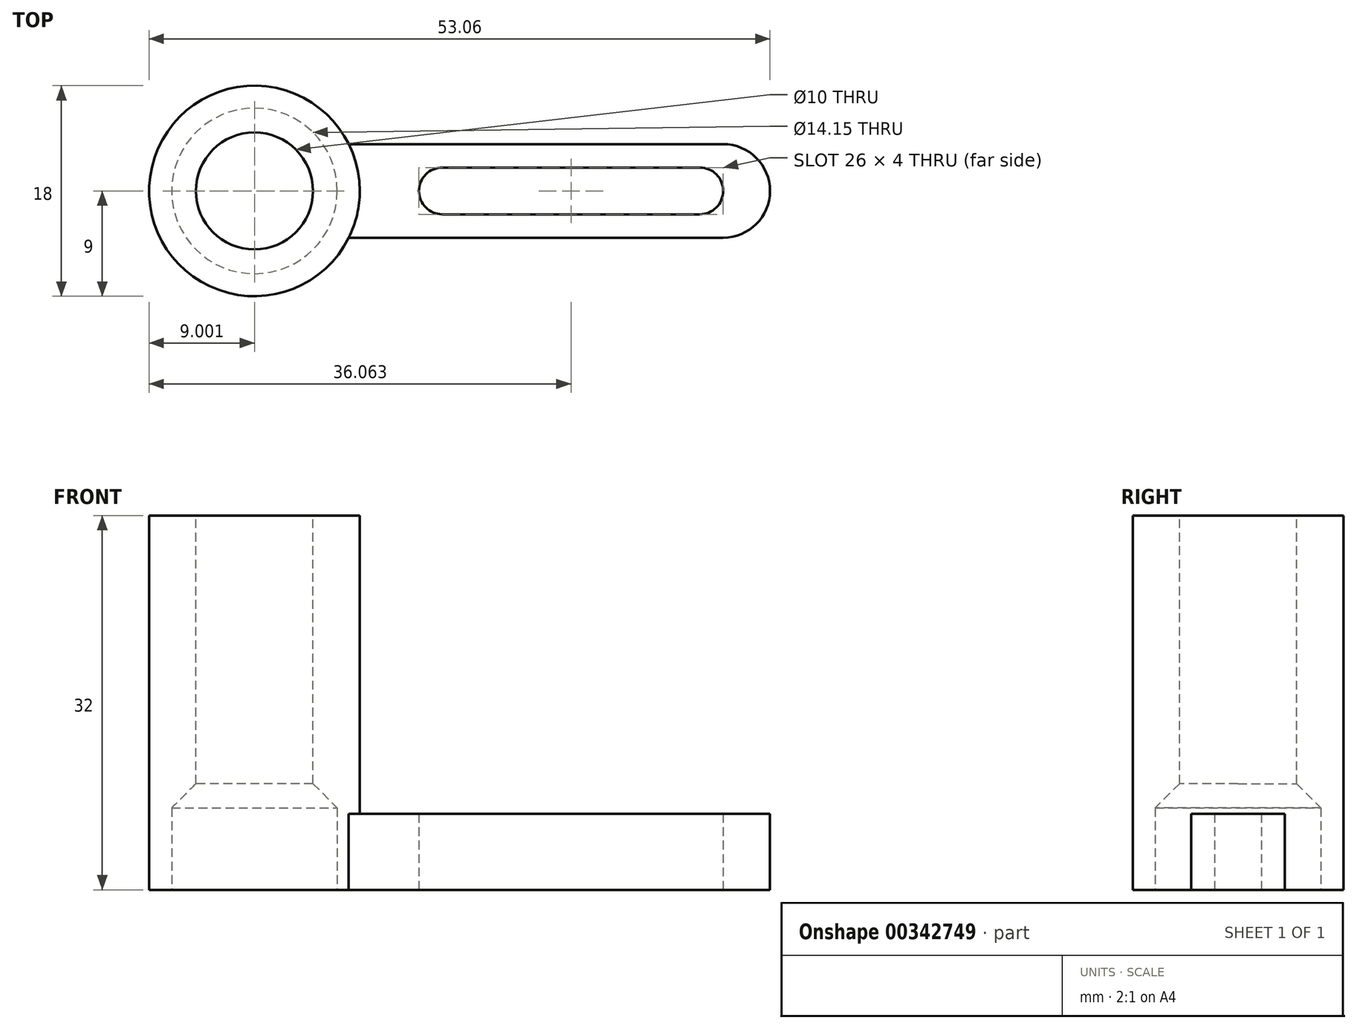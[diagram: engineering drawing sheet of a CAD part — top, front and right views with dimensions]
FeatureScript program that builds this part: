
annotation { "Feature Type Name" : "Feature", "Feature Type Description" : "" }
export const myFeature = defineFeature(function(context is Context, id is Id, definition is map)
    precondition{}
    {
        {
            var Q0;
            Q0=qCreatedBy(makeId("Top.planeOp"),FACE);
            var sketch = newSketch(context, id + "F0", { "sketchPlane" : qUnion([Q0])});
            skLineSegment(sketch, "E0", {"start": v(-60.74, 4) * mm, "end": v(-28.74, 4) * mm});
            skArc(sketch, "E1", {"start": v(-28.74, 4) * mm, "mid": v(-25.9, 2.83) * mm, "end": v(-24.74, 0) * mm});
            skLineSegment(sketch, "E2", {"start": v(-52.74, 2) * mm, "end": v(-30.74, 2) * mm});
            skArc(sketch, "E3", {"start": v(-54.74, 0) * mm, "mid": v(-54.15, 1.41) * mm, "end": v(-52.74, 2) * mm});
            skArc(sketch, "E4", {"start": v(-28.74, 0) * mm, "mid": v(-29.32, 1.41) * mm, "end": v(-30.74, 2) * mm});
            skArc(sketch, "E5", {"start": v(-60.74, 4) * mm, "mid": v(-70.85, 8.76) * mm, "end": v(-77.8, 0) * mm});
            skArc(sketch, "E6.MirrorCS", {"start": v(-60.74, -4) * mm, "mid": v(-70.85, -8.76) * mm, "end": v(-77.8, 0) * mm});
            skLineSegment(sketch, "E7.MirrorCS", {"start": v(-60.74, -4) * mm, "end": v(-28.74, -4) * mm});
            skArc(sketch, "E8.MirrorCS", {"start": v(-28.74, -4) * mm, "mid": v(-25.9, -2.83) * mm, "end": v(-24.74, 0) * mm});
            skArc(sketch, "E9.MirrorCS", {"start": v(-28.74, 0) * mm, "mid": v(-29.32, -1.41) * mm, "end": v(-30.74, -2) * mm});
            skLineSegment(sketch, "E10.MirrorCS", {"start": v(-52.74, -2) * mm, "end": v(-30.74, -2) * mm});
            skArc(sketch, "E11.MirrorCS", {"start": v(-54.74, 0) * mm, "mid": v(-54.15, -1.41) * mm, "end": v(-52.74, -2) * mm});
            skSolve(sketch);
        }
        {
            var Q0;
            Q0=makeQuery(id+"F0.imprint","IMPRINT",FACE,{"disambiguationData":[TD([[makeQuery(id+"F0.imprint","IMPRINT",EDGE,{"derivedFrom":sQuery(id+"F0.wireOp",EDGE,"E0")}),-1.0]])]});
            extrude(context, id + "F1", {"entities" : qUnion([Q0]), "depth" : 6.5 * mm});
        }
        {
            var Q0;
            Q0=makeQuery(id+"F1.opExtrude","CAP_FACE",FACE,{"disambiguationData":[OSD([sQuery(id+"F0.wireOp",EDGE,"E0"),sQuery(id+"F0.wireOp",EDGE,"E1"),sQuery(id+"F0.wireOp",EDGE,"E2"),sQuery(id+"F0.wireOp",EDGE,"E3"),sQuery(id+"F0.wireOp",EDGE,"E4"),sQuery(id+"F0.wireOp",EDGE,"E5"),sQuery(id+"F0.wireOp",EDGE,"E6.MirrorCS"),sQuery(id+"F0.wireOp",EDGE,"E7.MirrorCS"),sQuery(id+"F0.wireOp",EDGE,"E8.MirrorCS"),sQuery(id+"F0.wireOp",EDGE,"E9.MirrorCS"),sQuery(id+"F0.wireOp",EDGE,"E10.MirrorCS"),sQuery(id+"F0.wireOp",EDGE,"E11.MirrorCS")])],"isStart":false});
            var sketch = newSketch(context, id + "F2", { "sketchPlane" : qUnion([Q0])});
            skCircle(sketch, "E12", {"center": v(-68.8, 0) * mm, "radius": 9 * mm});
            skSolve(sketch);
        }
        {
            var Q0;
            {var subQ0=sQuery(id+"F2.wireOp",EDGE,"E12");var subQ1=makeQuery(id+"F2.imprint","INTERSECT",VERTEX,{"derivedFrom":[makeQuery(id+"F1.opExtrude","CAP_EDGE",EDGE,{"disambiguationData":[OSD([sQuery(id+"F0.wireOp",EDGE,"E0")])],"isStart":false}),subQ0]});Q0=makeQuery(id+"F2.imprint","IMPRINT",FACE,{"disambiguationData":[TD([[makeQuery(id+"F2.imprint","IMPRINT",EDGE,{"disambiguationData":[TD([[subQ1,-1.0]])],"derivedFrom":subQ0}),1.0]])]});}
            extrude(context, id + "F3", {"entities" : qUnion([Q0]), "operationType" : NewBodyOperationType.ADD, "depth" : 25.5 * mm});
        }
        {
            var Q0;
            Q0=makeQuery(id+"F3.opExtrude","CAP_FACE",FACE,{"disambiguationData":[OSD([sQuery(id+"F2.wireOp",EDGE,"E12")])],"isStart":false});
            var sketch = newSketch(context, id + "F4", { "sketchPlane" : qUnion([Q0])});
            skCircle(sketch, "E13", {"center": v(-68.8, 0) * mm, "radius": 5 * mm});
            skSolve(sketch);
        }
        {
            var Q0;
            Q0=makeQuery(id+"F4.imprint","IMPRINT",FACE,{"disambiguationData":[TD([[makeQuery(id+"F4.imprint","IMPRINT",EDGE,{"derivedFrom":sQuery(id+"F4.wireOp",EDGE,"E13")}),1.0]])]});
            var Q1;
            Q1=makeQuery(id+"F1.opExtrude","CAP_FACE",FACE,{"disambiguationData":[OSD([sQuery(id+"F0.wireOp",EDGE,"E0"),sQuery(id+"F0.wireOp",EDGE,"E1"),sQuery(id+"F0.wireOp",EDGE,"E2"),sQuery(id+"F0.wireOp",EDGE,"E3"),sQuery(id+"F0.wireOp",EDGE,"E4"),sQuery(id+"F0.wireOp",EDGE,"E5"),sQuery(id+"F0.wireOp",EDGE,"E6.MirrorCS"),sQuery(id+"F0.wireOp",EDGE,"E7.MirrorCS"),sQuery(id+"F0.wireOp",EDGE,"E8.MirrorCS"),sQuery(id+"F0.wireOp",EDGE,"E9.MirrorCS"),sQuery(id+"F0.wireOp",EDGE,"E10.MirrorCS"),sQuery(id+"F0.wireOp",EDGE,"E11.MirrorCS")])],"isStart":true});
            var Q2;
            Q2=makeQuery(id+"F1.opExtrude","SWEPT_BODY",BODY,{"disambiguationData":[OSD([sQuery(id+"F0.wireOp",EDGE,"E0"),sQuery(id+"F0.wireOp",EDGE,"E1"),sQuery(id+"F0.wireOp",EDGE,"E2"),sQuery(id+"F0.wireOp",EDGE,"E3"),sQuery(id+"F0.wireOp",EDGE,"E4"),sQuery(id+"F0.wireOp",EDGE,"E5"),sQuery(id+"F0.wireOp",EDGE,"E6.MirrorCS"),sQuery(id+"F0.wireOp",EDGE,"E7.MirrorCS"),sQuery(id+"F0.wireOp",EDGE,"E8.MirrorCS"),sQuery(id+"F0.wireOp",EDGE,"E9.MirrorCS"),sQuery(id+"F0.wireOp",EDGE,"E10.MirrorCS"),sQuery(id+"F0.wireOp",EDGE,"E11.MirrorCS")])]});
            extrude(context, id + "F5", {"entities" : qUnion([Q0]), "operationType" : NewBodyOperationType.REMOVE, "endBound" : BoundingType.UP_TO_NEXT, "oppositeDirection" : true, "endBoundEntityFace" : qUnion([Q1]), "endBoundEntityBody" : qUnion([Q2]), "depth" : 34.3 * mm});
        }
        {
            var Q0;
            Q0=makeQuery(id+"F1.opExtrude","CAP_FACE",FACE,{"disambiguationData":[OSD([sQuery(id+"F0.wireOp",EDGE,"E0"),sQuery(id+"F0.wireOp",EDGE,"E1"),sQuery(id+"F0.wireOp",EDGE,"E2"),sQuery(id+"F0.wireOp",EDGE,"E3"),sQuery(id+"F0.wireOp",EDGE,"E4"),sQuery(id+"F0.wireOp",EDGE,"E5"),sQuery(id+"F0.wireOp",EDGE,"E6.MirrorCS"),sQuery(id+"F0.wireOp",EDGE,"E7.MirrorCS"),sQuery(id+"F0.wireOp",EDGE,"E8.MirrorCS"),sQuery(id+"F0.wireOp",EDGE,"E9.MirrorCS"),sQuery(id+"F0.wireOp",EDGE,"E10.MirrorCS"),sQuery(id+"F0.wireOp",EDGE,"E11.MirrorCS")])],"isStart":true});
            var sketch = newSketch(context, id + "F6", { "sketchPlane" : qUnion([Q0])});
            skCircle(sketch, "E14", {"center": v(-68.8, 0) * mm, "radius": 7.08 * mm});
            skSolve(sketch);
        }
        {
            var Q0;
            Q0=makeQuery(id+"F6.imprint","IMPRINT",FACE,{"disambiguationData":[TD([[makeQuery(id+"F6.imprint","IMPRINT",EDGE,{"derivedFrom":sQuery(id+"F6.wireOp",EDGE,"E14")}),1.0]])]});
            extrude(context, id + "F7", {"entities" : qUnion([Q0]), "operationType" : NewBodyOperationType.REMOVE, "oppositeDirection" : true, "depth" : 12 * mm});
        }
        {
            var Q0;
            Q0=makeQuery(id+"F7.boolean.opBoolean","COPY",EDGE,{"derivedFrom":makeQuery(id+"F7.opExtrude","CAP_EDGE",EDGE,{"disambiguationData":[OSD([sQuery(id+"F6.wireOp",EDGE,"E14")])],"isStart":false})});
            chamfer(context, id + "F8", {"entities" : qUnion([Q0]), "width" : 5 * mm, "tangentPropagation" : true});
        }
    });
